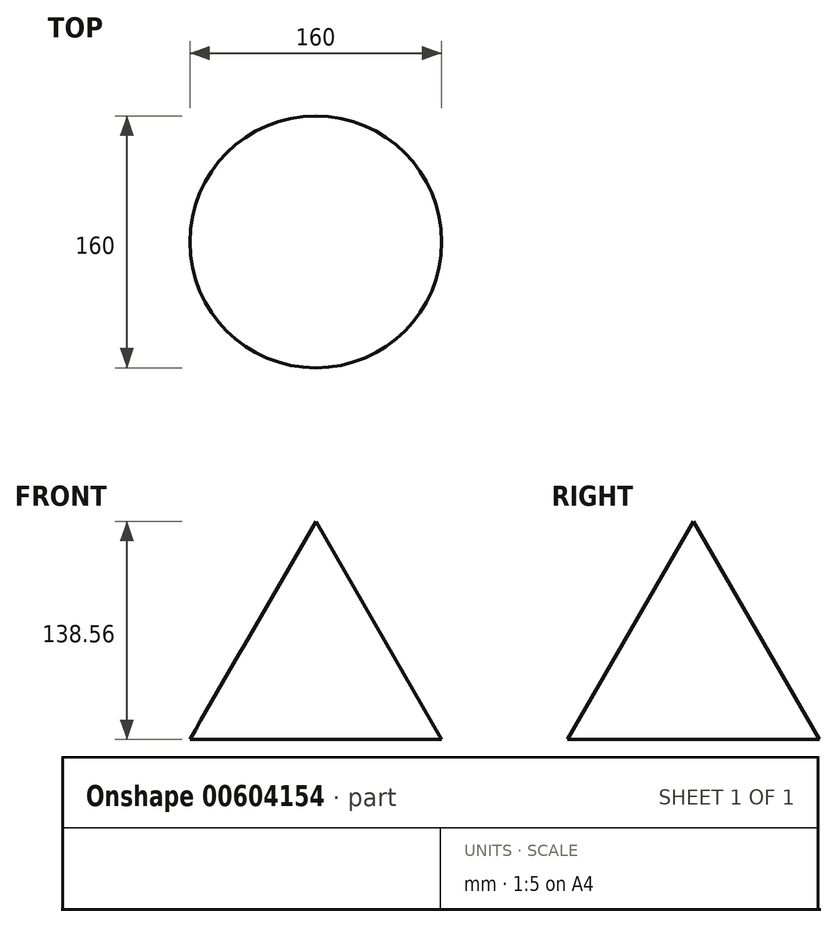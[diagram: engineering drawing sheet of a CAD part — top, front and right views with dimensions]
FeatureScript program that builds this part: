
annotation { "Feature Type Name" : "Feature", "Feature Type Description" : "" }
export const myFeature = defineFeature(function(context is Context, id is Id, definition is map)
    precondition{}
    {
        {
            var Q0;
            Q0=qCreatedBy(makeId("Front.planeOp"),FACE);
            var sketch = newSketch(context, id + "F0", { "sketchPlane" : qUnion([Q0])});
            skLineSegment(sketch, "E0", {"start": v(0, 138.56) * mm, "end": v(0, 0) * mm});
            skLineSegment(sketch, "E1", {"start": v(0, 0) * mm, "end": v(80, 0) * mm});
            skLineSegment(sketch, "E2", {"start": v(80, 0) * mm, "end": v(0, 138.56) * mm});
            skSolve(sketch);
        }
        {
            var Q0;
            Q0=makeQuery(id+"F0.imprint","IMPRINT",FACE,{"disambiguationData":[TD([[makeQuery(id+"F0.imprint","IMPRINT",EDGE,{"derivedFrom":sQuery(id+"F0.wireOp",EDGE,"E0")}),1.0]])]});
            var Q1;
            Q1=sQuery(id+"F0.wireOp",EDGE,"E0");
            revolve(context, id + "F1", {"surfaceOperationType" : NewSurfaceOperationType.NEW, "entities" : qUnion([Q0]), "axis" : qUnion([Q1]), "revolveType" : RevolveType.FULL});
        }
    });
